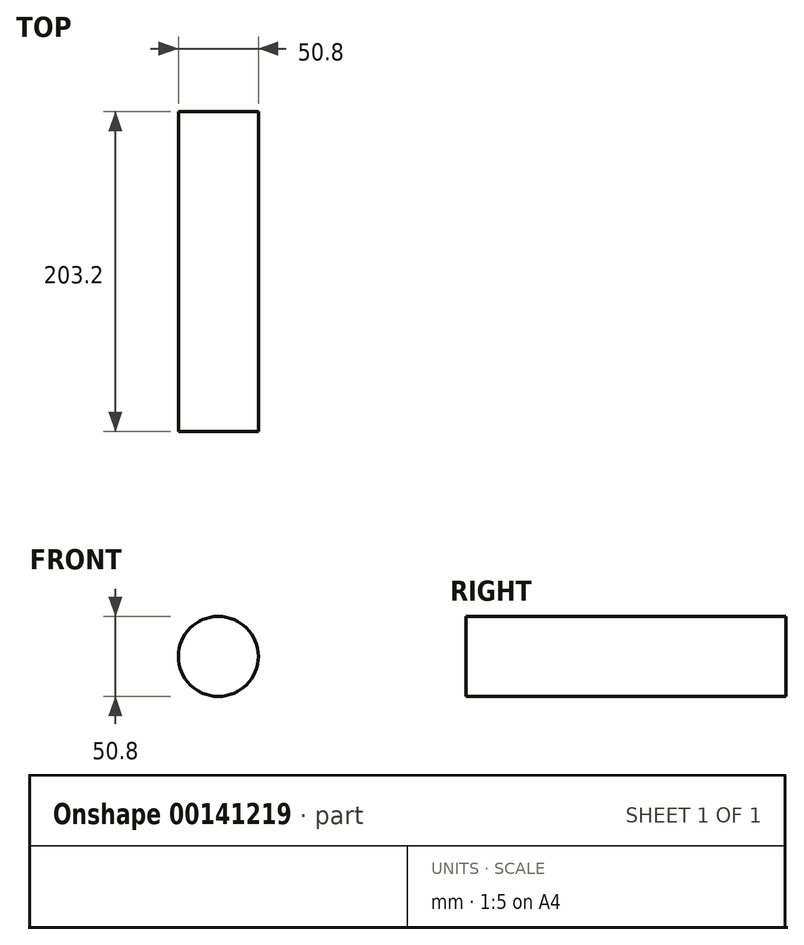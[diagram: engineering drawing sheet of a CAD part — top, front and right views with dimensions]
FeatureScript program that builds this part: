
annotation { "Feature Type Name" : "Feature", "Feature Type Description" : "" }
export const myFeature = defineFeature(function(context is Context, id is Id, definition is map)
    precondition{}
    {
        {
            var Q0;
            Q0=qCreatedBy(makeId("Front.planeOp"),FACE);
            var sketch = newSketch(context, id + "F0", { "sketchPlane" : qUnion([Q0])});
            skCircle(sketch, "E0", {"center": v(-23.26, 38.85) * mm, "radius": 25.4 * mm});
            skSolve(sketch);
        }
        {
            var Q0;
            Q0 = qSketchRegion(id + "F0", true);
            extrude(context, id + "F1", {"entities" : qUnion([Q0]), "depth" : 203.2 * mm});
        }
    });
